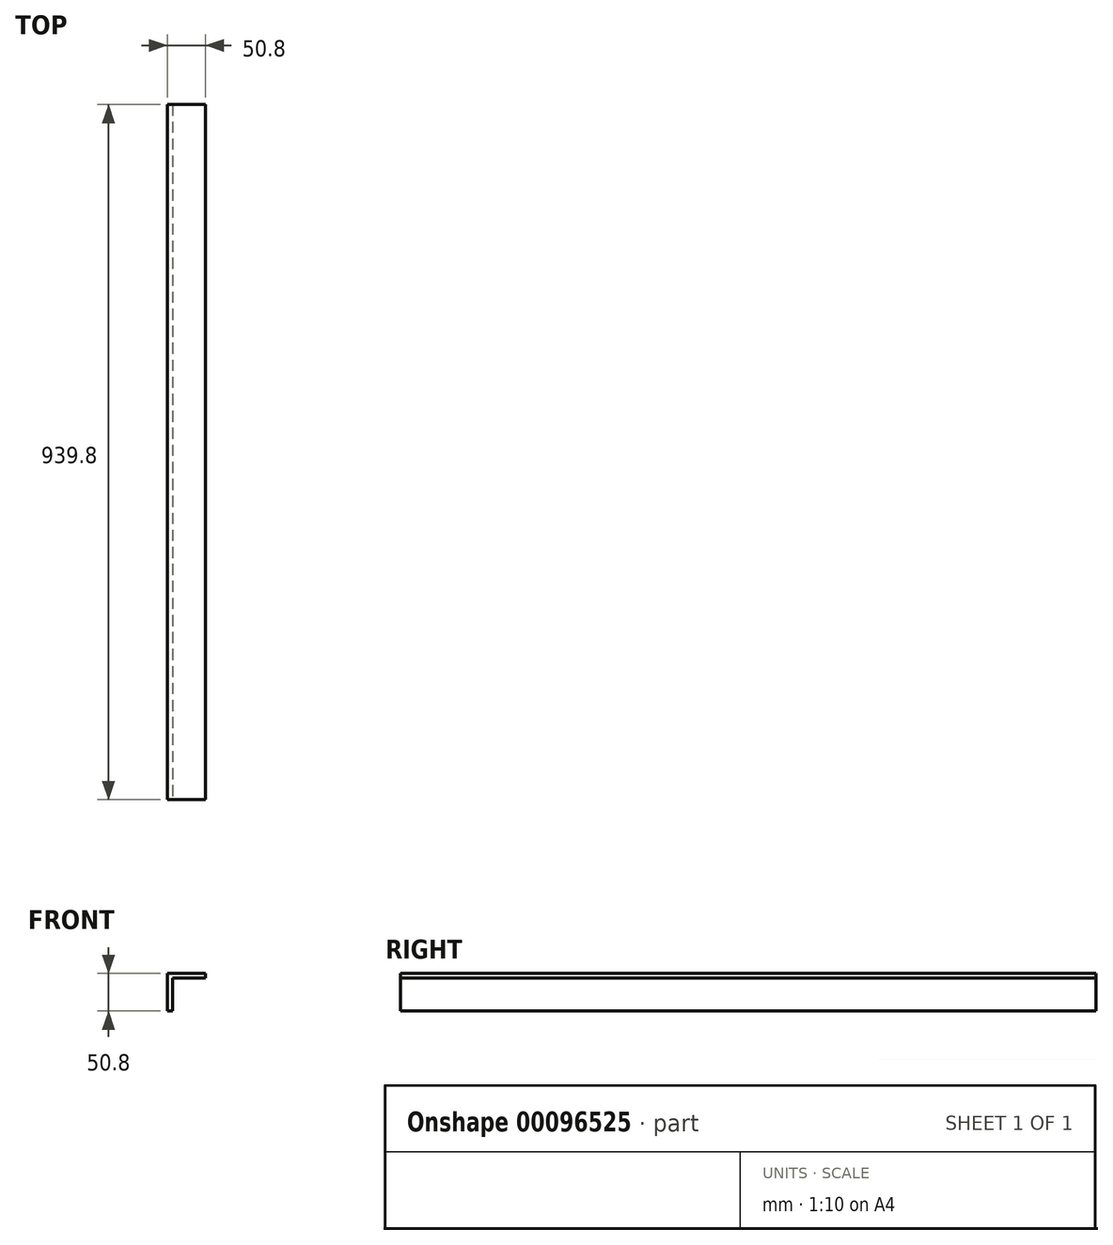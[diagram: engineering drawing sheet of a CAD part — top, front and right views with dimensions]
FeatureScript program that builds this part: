
annotation { "Feature Type Name" : "Feature", "Feature Type Description" : "" }
export const myFeature = defineFeature(function(context is Context, id is Id, definition is map)
    precondition{}
    {
        {
            var Q0;
            Q0=qCreatedBy(makeId("Front.planeOp"),FACE);
            var sketch = newSketch(context, id + "F0", { "sketchPlane" : qUnion([Q0])});
            skLineSegment(sketch, "E0", {"start": v(0, 0) * mm, "end": v(-50.8, 0) * mm});
            skLineSegment(sketch, "E1", {"start": v(-50.8, 0) * mm, "end": v(-50.8, -50.8) * mm});
            skLineSegment(sketch, "E2.0", {"start": v(-44.45, -6.35) * mm, "end": v(-44.45, -50.8) * mm});
            skLineSegment(sketch, "E2.1", {"start": v(0, -6.35) * mm, "end": v(-44.45, -6.35) * mm});
            skLineSegment(sketch, "E3", {"start": v(0, 0) * mm, "end": v(0, -6.35) * mm});
            skLineSegment(sketch, "E4", {"start": v(-44.45, -50.8) * mm, "end": v(-50.8, -50.8) * mm});
            skSolve(sketch);
        }
        {
            var Q0;
            Q0=qSketchRegion(id+"F0",true);
            extrude(context, id + "F1", {"entities" : qUnion([Q0]), "oppositeDirection" : true, "depth" : 939.8 * mm});
        }
    });
